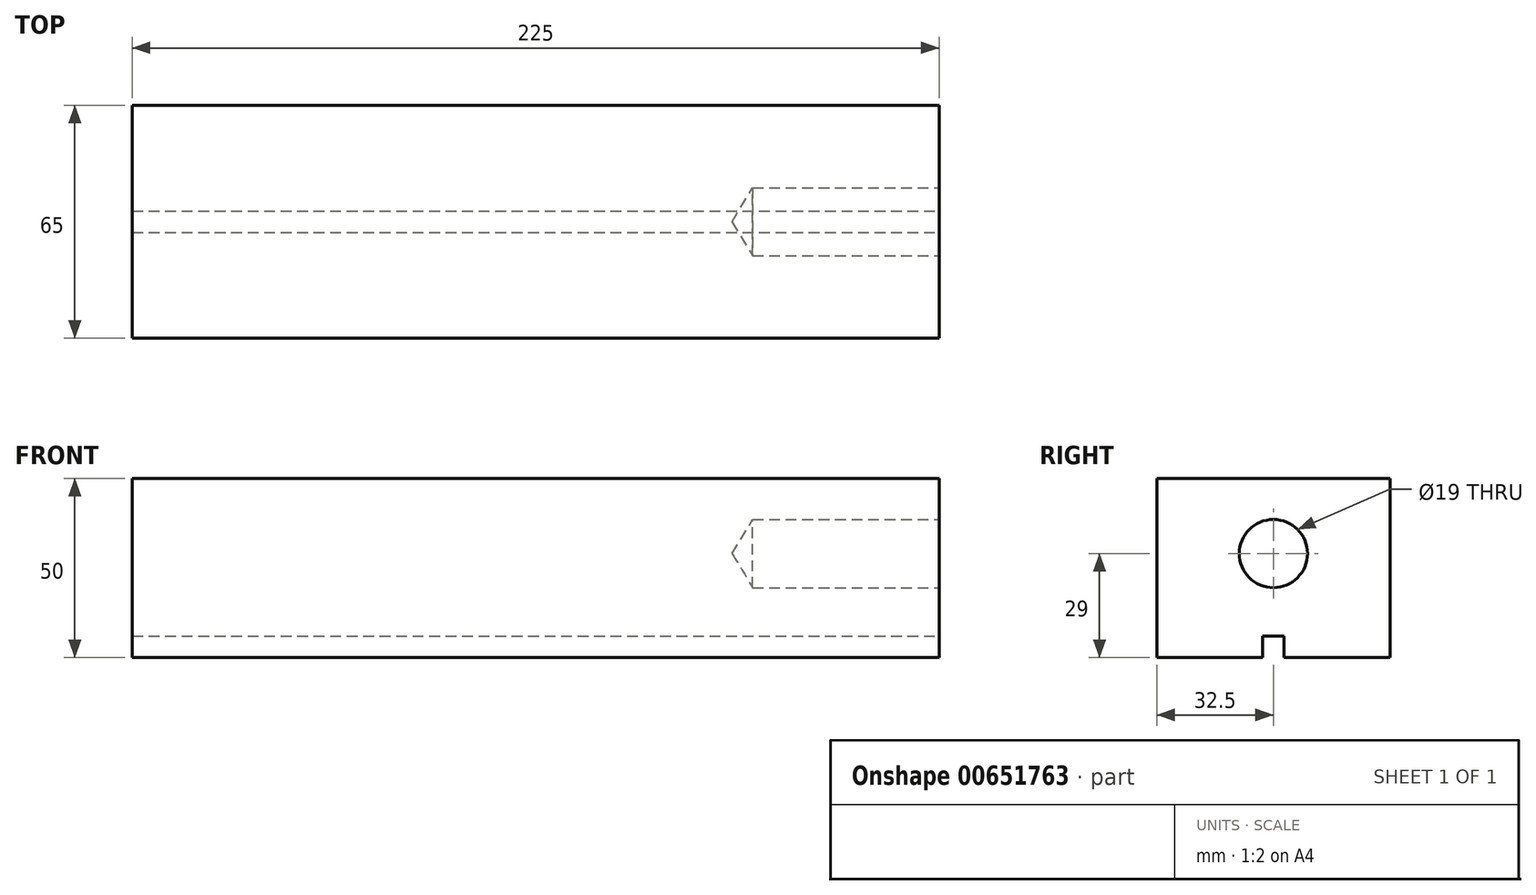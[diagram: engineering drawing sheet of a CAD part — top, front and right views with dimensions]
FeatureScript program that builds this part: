
annotation { "Feature Type Name" : "Feature", "Feature Type Description" : "" }
export const myFeature = defineFeature(function(context is Context, id is Id, definition is map)
    precondition{}
    {
        {
            var Q0;
            Q0=qCreatedBy(makeId("Right.planeOp"),FACE);
            var sketch = newSketch(context, id + "F0", { "sketchPlane" : qUnion([Q0])});
            skLineSegment(sketch, "E0", {"start": v(0, 6) * mm, "end": v(0, 50) * mm});
            skLineSegment(sketch, "E1", {"start": v(0, 50) * mm, "end": v(32.5, 50) * mm});
            skLineSegment(sketch, "E2", {"start": v(32.5, 50) * mm, "end": v(32.5, 0) * mm});
            skLineSegment(sketch, "E3", {"start": v(32.5, 0) * mm, "end": v(3, 0) * mm});
            skLineSegment(sketch, "E4", {"start": v(0, 6) * mm, "end": v(3, 6) * mm});
            skLineSegment(sketch, "E5", {"start": v(3, 6) * mm, "end": v(3, 0) * mm});
            skPoint(sketch, "E6", {"position": v(0, 29) * mm});
            skSolve(sketch);
        }
        {
            var Q0;
            Q0=makeQuery(id+"F0.imprint","IMPRINT",FACE,{"disambiguationData":[TD([[makeQuery(id+"F0.imprint","IMPRINT",EDGE,{"derivedFrom":sQuery(id+"F0.wireOp",EDGE,"E0")}),-1.0]])]});
            extrude(context, id + "F1", {"entities" : qUnion([Q0]), "oppositeDirection" : true, "depth" : 225 * mm, "offsetDistance" : 25 * mm});
        }
        {
            var Q0;
            Q0=makeQuery(id+"F1.opExtrude","CAP_FACE",FACE,{"disambiguationData":[OSD([sQuery(id+"F0.wireOp",EDGE,"E0"),sQuery(id+"F0.wireOp",EDGE,"E1"),sQuery(id+"F0.wireOp",EDGE,"E2"),sQuery(id+"F0.wireOp",EDGE,"E3"),sQuery(id+"F0.wireOp",EDGE,"E4"),sQuery(id+"F0.wireOp",EDGE,"E5")])],"isStart":true});
            var sketch = newSketch(context, id + "F2", { "sketchPlane" : qUnion([Q0])});
            skPoint(sketch, "E7", {"position": v(0, 29) * mm});
            skSolve(sketch);
        }
        {
            var Q0;
            Q0=sQuery(id+"F2.wireOp",VERTEX,"E7");
            var Q1;
            Q1=makeQuery(id+"F1.opExtrude","SWEPT_BODY",BODY,{"disambiguationData":[OSD([sQuery(id+"F0.wireOp",EDGE,"E0"),sQuery(id+"F0.wireOp",EDGE,"E1"),sQuery(id+"F0.wireOp",EDGE,"E2"),sQuery(id+"F0.wireOp",EDGE,"E3"),sQuery(id+"F0.wireOp",EDGE,"E4"),sQuery(id+"F0.wireOp",EDGE,"E5")])]});
            hole(context, id + "F3", {"style" : HoleStyle.SIMPLE, "endStyle" : HoleEndStyle.BLIND, "holeDiameter" : 19 * mm, "majorDiameter" : 5 * mm, "holeDepth" : 52 * mm, "isTappedThrough" : true, "tappedDepth" : 12 * mm, "tapClearance" : 3, "startFromSketch" : true, "locations" : qUnion([Q0]), "scope" : qUnion([Q1])});
        }
        {
            var Q0;
            Q0=makeQuery(id+"F1.opExtrude","SWEPT_BODY",BODY,{"disambiguationData":[OSD([sQuery(id+"F0.wireOp",EDGE,"E0"),sQuery(id+"F0.wireOp",EDGE,"E1"),sQuery(id+"F0.wireOp",EDGE,"E2"),sQuery(id+"F0.wireOp",EDGE,"E3"),sQuery(id+"F0.wireOp",EDGE,"E4"),sQuery(id+"F0.wireOp",EDGE,"E5")])]});
            var Q1;
            Q1=makeQuery(id+"F1.opExtrude","SWEPT_FACE",FACE,{"disambiguationData":[OSD([sQuery(id+"F0.wireOp",EDGE,"E0")])]});
            mirror(context, id + "F4", {"operationType" : NewBodyOperationType.ADD, "entities" : qUnion([Q0]), "mirrorPlane" : qUnion([Q1])});
        }
    });
